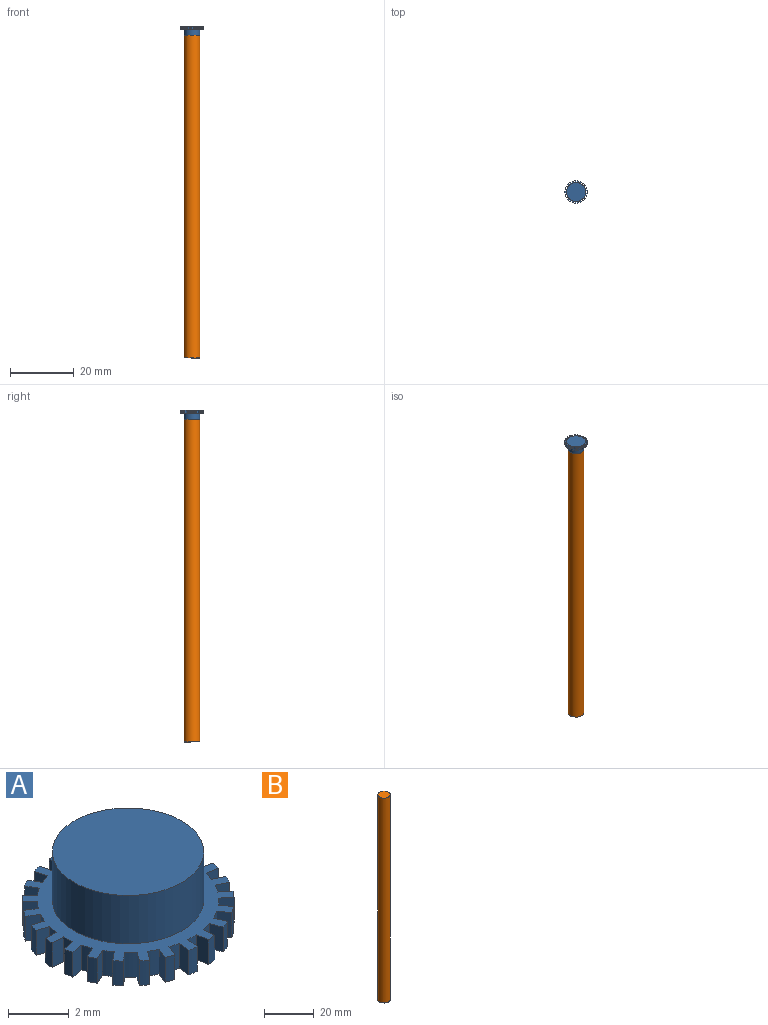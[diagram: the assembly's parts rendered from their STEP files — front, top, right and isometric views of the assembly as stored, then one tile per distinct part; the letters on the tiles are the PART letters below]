
ASSEMBLY  parts=2 mates=1
PART A: 104 faces, bbox 7x7x3 mm
  f0: cylinder r=3.5mm len=1mm, axis (0,0,-1), area 0.4mm2, adj f1,f99,f100,f101
  f1: plane 1x0.5mm, normal (-0.06,-1,0), area 0.5mm2, adj f0,f2,f100,f101
  f2: cylinder r=3mm len=1mm, axis (0,0,-1), area 0.4mm2, adj f1,f3,f100,f101
  f3: plane 1x0.49mm, normal (-0.19,0.98,0), area 0.5mm2, adj f2,f4,f100,f101
  f4: cylinder r=3.5mm len=1mm, axis (0,0,-1), area 0.4mm2, adj f3,f5,f100,f101
  f5: plane 1x0.49mm, normal (0.19,-0.98,0), area 0.5mm2, adj f4,f6,f100,f101
  f6: cylinder r=3mm len=1mm, axis (0,0,-1), area 0.4mm2, adj f5,f7,f100,f101
  f7: plane 1x0.45mm, normal (-0.43,0.9,0), area 0.5mm2, adj f6,f8,f100,f101
  f8: cylinder r=3.5mm len=1mm, axis (0,0,-1), area 0.4mm2, adj f7,f9,f100,f101
  f9: plane 1x0.45mm, normal (0.43,-0.9,0), area 0.5mm2, adj f8,f10,f100,f101
  f10: cylinder r=3mm len=1mm, axis (0,0,-1), area 0.4mm2, adj f9,f11,f100,f101
  f11: plane 1x0.39mm, normal (-0.64,0.77,0), area 0.5mm2, adj f10,f12,f100,f101
  f12: cylinder r=3.5mm len=1mm, axis (0,0,-1), area 0.4mm2, adj f11,f13,f100,f101
  f13: plane 1x0.39mm, normal (0.64,-0.77,0), area 0.5mm2, adj f12,f14,f100,f101
  f14: cylinder r=3mm len=1mm, axis (0,0,-1), area 0.4mm2, adj f13,f15,f100,f101
  f15: plane 1x0.4mm, normal (-0.81,0.59,0), area 0.5mm2, adj f14,f16,f100,f101
  f16: cylinder r=3.5mm len=1mm, axis (0,0,-1), area 0.4mm2, adj f15,f17,f100,f101
  f17: plane 1x0.4mm, normal (0.81,-0.59,0), area 0.5mm2, adj f16,f18,f100,f101
  f18: cylinder r=3mm len=1mm, axis (0,0,-1), area 0.4mm2, adj f17,f19,f100,f101
  f19: plane 1x0.47mm, normal (-0.93,0.37,0), area 0.5mm2, adj f18,f20,f100,f101
  f20: cylinder r=3.5mm len=1mm, axis (0,0,-1), area 0.4mm2, adj f19,f21,f100,f101
  f21: plane 1x0.47mm, normal (0.93,-0.37,0), area 0.5mm2, adj f20,f22,f100,f101
  f22: cylinder r=3mm len=1mm, axis (0,0,-1), area 0.4mm2, adj f21,f23,f100,f101
  f23: plane 1x0.5mm, normal (-0.99,0.13,0), area 0.5mm2, adj f22,f24,f100,f101
  f24: cylinder r=3.5mm len=1mm, axis (0,0,-1), area 0.4mm2, adj f23,f25,f100,f101
  f25: plane 1x0.5mm, normal (0.99,-0.13,0), area 0.5mm2, adj f24,f26,f100,f101
  f26: cylinder r=3mm len=1mm, axis (0,0,-1), area 0.4mm2, adj f25,f27,f100,f101
  f27: plane 1x0.5mm, normal (-0.99,-0.13,0), area 0.5mm2, adj f26,f28,f100,f101
  f28: cylinder r=3.5mm len=1mm, axis (0,0,-1), area 0.4mm2, adj f27,f29,f100,f101
  f29: plane 1x0.5mm, normal (0.99,0.13,0), area 0.5mm2, adj f28,f30,f100,f101
  f30: cylinder r=3mm len=1mm, axis (0,0,-1), area 0.4mm2, adj f29,f31,f100,f101
  f31: plane 1x0.47mm, normal (-0.93,-0.37,0), area 0.5mm2, adj f30,f32,f100,f101
  f32: cylinder r=3.5mm len=1mm, axis (0,0,-1), area 0.4mm2, adj f31,f33,f100,f101
  f33: plane 1x0.47mm, normal (0.93,0.37,0), area 0.5mm2, adj f32,f34,f100,f101
  f34: cylinder r=3mm len=1mm, axis (0,0,-1), area 0.4mm2, adj f33,f35,f100,f101
  f35: plane 1x0.4mm, normal (-0.81,-0.59,0), area 0.5mm2, adj f34,f36,f100,f101
  f36: cylinder r=3.5mm len=1mm, axis (0,0,-1), area 0.4mm2, adj f35,f37,f100,f101
  f37: plane 1x0.4mm, normal (0.81,0.59,0), area 0.5mm2, adj f36,f38,f100,f101
  f38: cylinder r=3mm len=1mm, axis (0,0,-1), area 0.4mm2, adj f37,f39,f100,f101
  f39: plane 1x0.39mm, normal (-0.64,-0.77,0), area 0.5mm2, adj f38,f40,f100,f101
  f40: cylinder r=3.5mm len=1mm, axis (0,0,-1), area 0.4mm2, adj f39,f41,f100,f101
  f41: plane 1x0.39mm, normal (0.64,0.77,0), area 0.5mm2, adj f40,f42,f100,f101
  f42: cylinder r=3mm len=1mm, axis (0,0,-1), area 0.4mm2, adj f41,f43,f100,f101
  f43: plane 1x0.45mm, normal (-0.43,-0.9,0), area 0.5mm2, adj f42,f44,f100,f101
  f44: cylinder r=3.5mm len=1mm, axis (0,0,-1), area 0.4mm2, adj f43,f45,f100,f101
  f45: plane 1x0.45mm, normal (0.43,0.9,0), area 0.5mm2, adj f44,f46,f100,f101
  f46: cylinder r=3mm len=1mm, axis (0,0,-1), area 0.4mm2, adj f45,f47,f100,f101
  f47: plane 1x0.49mm, normal (-0.19,-0.98,0), area 0.5mm2, adj f46,f48,f100,f101
  f48: cylinder r=3.5mm len=1mm, axis (0,0,-1), area 0.4mm2, adj f47,f49,f100,f101
  f49: plane 1x0.49mm, normal (0.19,0.98,0), area 0.5mm2, adj f48,f50,f100,f101
  f50: cylinder r=3mm len=1mm, axis (0,0,-1), area 0.4mm2, adj f49,f51,f100,f101
  f51: plane 1x0.5mm, normal (0.06,-1,0), area 0.5mm2, adj f50,f52,f100,f101
  f52: cylinder r=3.5mm len=1mm, axis (0,0,-1), area 0.4mm2, adj f51,f53,f100,f101
  f53: plane 1x0.5mm, normal (-0.06,1,0), area 0.5mm2, adj f52,f54,f100,f101
  f54: cylinder r=3mm len=1mm, axis (0,0,-1), area 0.4mm2, adj f53,f55,f100,f101
  f55: plane 1x0.48mm, normal (0.31,-0.95,0), area 0.5mm2, adj f54,f56,f100,f101
  f56: cylinder r=3.5mm len=1mm, axis (0,0,-1), area 0.4mm2, adj f55,f57,f100,f101
  f57: plane 1x0.48mm, normal (-0.31,0.95,0), area 0.5mm2, adj f56,f58,f100,f101
  f58: cylinder r=3mm len=1mm, axis (0,0,-1), area 0.4mm2, adj f57,f59,f100,f101
  f59: plane 1x0.42mm, normal (0.54,-0.84,0), area 0.5mm2, adj f58,f60,f100,f101
  f60: cylinder r=3.5mm len=1mm, axis (0,0,-1), area 0.4mm2, adj f59,f61,f100,f101
  f61: plane 1x0.42mm, normal (-0.54,0.84,0), area 0.5mm2, adj f60,f62,f100,f101
  f62: cylinder r=3mm len=1mm, axis (0,0,-1), area 0.4mm2, adj f61,f63,f100,f101
  f63: plane 1x0.36mm, normal (0.73,-0.68,0), area 0.5mm2, adj f62,f64,f100,f101
  f64: cylinder r=3.5mm len=1mm, axis (0,0,-1), area 0.4mm2, adj f63,f65,f100,f101
  f65: plane 1x0.36mm, normal (-0.73,0.68,0), area 0.5mm2, adj f64,f66,f100,f101
  f66: cylinder r=3mm len=1mm, axis (0,0,-1), area 0.4mm2, adj f65,f67,f100,f101
  f67: plane 1x0.44mm, normal (0.88,-0.48,0), area 0.5mm2, adj f66,f68,f100,f101
  f68: cylinder r=3.5mm len=1mm, axis (0,0,-1), area 0.4mm2, adj f67,f69,f100,f101
  f69: plane 1x0.44mm, normal (-0.88,0.48,0), area 0.5mm2, adj f68,f70,f100,f101
  f70: cylinder r=3mm len=1mm, axis (0,0,-1), area 0.4mm2, adj f69,f71,f100,f101
  f71: plane 1x0.48mm, normal (0.97,-0.25,0), area 0.5mm2, adj f70,f72,f100,f101
  f72: cylinder r=3.5mm len=1mm, axis (0,0,-1), area 0.4mm2, adj f71,f73,f100,f101
  f73: plane 1x0.48mm, normal (-0.97,0.25,0), area 0.5mm2, adj f72,f74,f100,f101
  f74: cylinder r=3mm len=1mm, axis (0,0,-1), area 0.4mm2, adj f73,f75,f100,f101
  f75: plane 1x0.5mm, normal (1,0,0), area 0.5mm2, adj f74,f76,f100,f101
  f76: cylinder r=3.5mm len=1mm, axis (0,0,-1), area 0.4mm2, adj f75,f77,f100,f101
  f77: plane 1x0.5mm, normal (-1,0,0), area 0.5mm2, adj f76,f78,f100,f101
  f78: cylinder r=3mm len=1mm, axis (0,0,-1), area 0.4mm2, adj f77,f79,f100,f101
  f79: plane 1x0.48mm, normal (0.97,0.25,0), area 0.5mm2, adj f78,f80,f100,f101
  f80: cylinder r=3.5mm len=1mm, axis (0,0,-1), area 0.4mm2, adj f79,f81,f100,f101
  f81: plane 1x0.48mm, normal (-0.97,-0.25,0), area 0.5mm2, adj f80,f82,f100,f101
  f82: cylinder r=3mm len=1mm, axis (0,0,-1), area 0.4mm2, adj f81,f83,f100,f101
  f83: plane 1x0.44mm, normal (0.88,0.48,0), area 0.5mm2, adj f82,f84,f100,f101
  f84: cylinder r=3.5mm len=1mm, axis (0,0,-1), area 0.4mm2, adj f83,f85,f100,f101
  f85: plane 1x0.44mm, normal (-0.88,-0.48,0), area 0.5mm2, adj f84,f86,f100,f101
  f86: cylinder r=3mm len=1mm, axis (0,0,-1), area 0.4mm2, adj f85,f87,f100,f101
  f87: plane 1x0.36mm, normal (0.73,0.68,0), area 0.5mm2, adj f86,f88,f100,f101
  f88: cylinder r=3.5mm len=1mm, axis (0,0,-1), area 0.4mm2, adj f87,f89,f100,f101
  f89: plane 1x0.36mm, normal (-0.73,-0.68,0), area 0.5mm2, adj f88,f90,f100,f101
  f90: cylinder r=3mm len=1mm, axis (0,0,-1), area 0.4mm2, adj f89,f91,f100,f101
  f91: plane 1x0.42mm, normal (0.54,0.84,0), area 0.5mm2, adj f90,f92,f100,f101
  f92: cylinder r=3.5mm len=1mm, axis (0,0,-1), area 0.4mm2, adj f91,f93,f100,f101
  f93: plane 1x0.42mm, normal (-0.54,-0.84,0), area 0.5mm2, adj f92,f94,f100,f101
  f94: cylinder r=3mm len=1mm, axis (0,0,-1), area 0.4mm2, adj f93,f95,f100,f101
  f95: plane 1x0.48mm, normal (0.31,0.95,0), area 0.5mm2, adj f94,f96,f100,f101
  f96: cylinder r=3.5mm len=1mm, axis (0,0,-1), area 0.4mm2, adj f95,f97,f100,f101
  f97: plane 1x0.48mm, normal (-0.31,-0.95,0), area 0.5mm2, adj f96,f98,f100,f101
  f98: cylinder r=3mm len=1mm, axis (0,0,-1), area 0.4mm2, adj f97,f99,f100,f101
  f99: plane 1x0.5mm, normal (0.06,1,0), area 0.5mm2, adj f0,f98,f100,f101
  f100: plane 7x6.99mm, normal (0,0,1), area 13mm2, adj f0,f1,f2,f3,f4,f5,f6,f7
  f101: plane 7x6.99mm, normal (0,0,-1), area 32.7mm2, adj f0,f1,f2,f3,f4,f5,f6,f7
  f102: cylinder r=2.5mm len=5mm, axis (0,0,-1), area 30.6mm2, adj f100,f103
  f103: plane 5x5mm, normal (0,0,1), area 19.6mm2, adj f102
PART B: 3 faces, bbox 5x5x101 mm
  f0: plane 5x5mm, normal (0,0,1), area 19.6mm2, adj f1
  f1: cylinder r=2.5mm len=101mm, axis (0,0,-1), area 1586.5mm2, adj f0,f2
  f2: plane 5x5mm, normal (0,0,-1), area 19.6mm2, adj f1
PLACE A rot(axis=(0.71,-0.71,0),180deg) t=(10,9.58,168.95)mm
PLACE B rot(axis=(0,0,-1),90deg) t=(0,-7.92,115)mm
MATE fastened B.f1 <-> A.f0  axis (0,0,1) through (0,-0.42,166)mm
